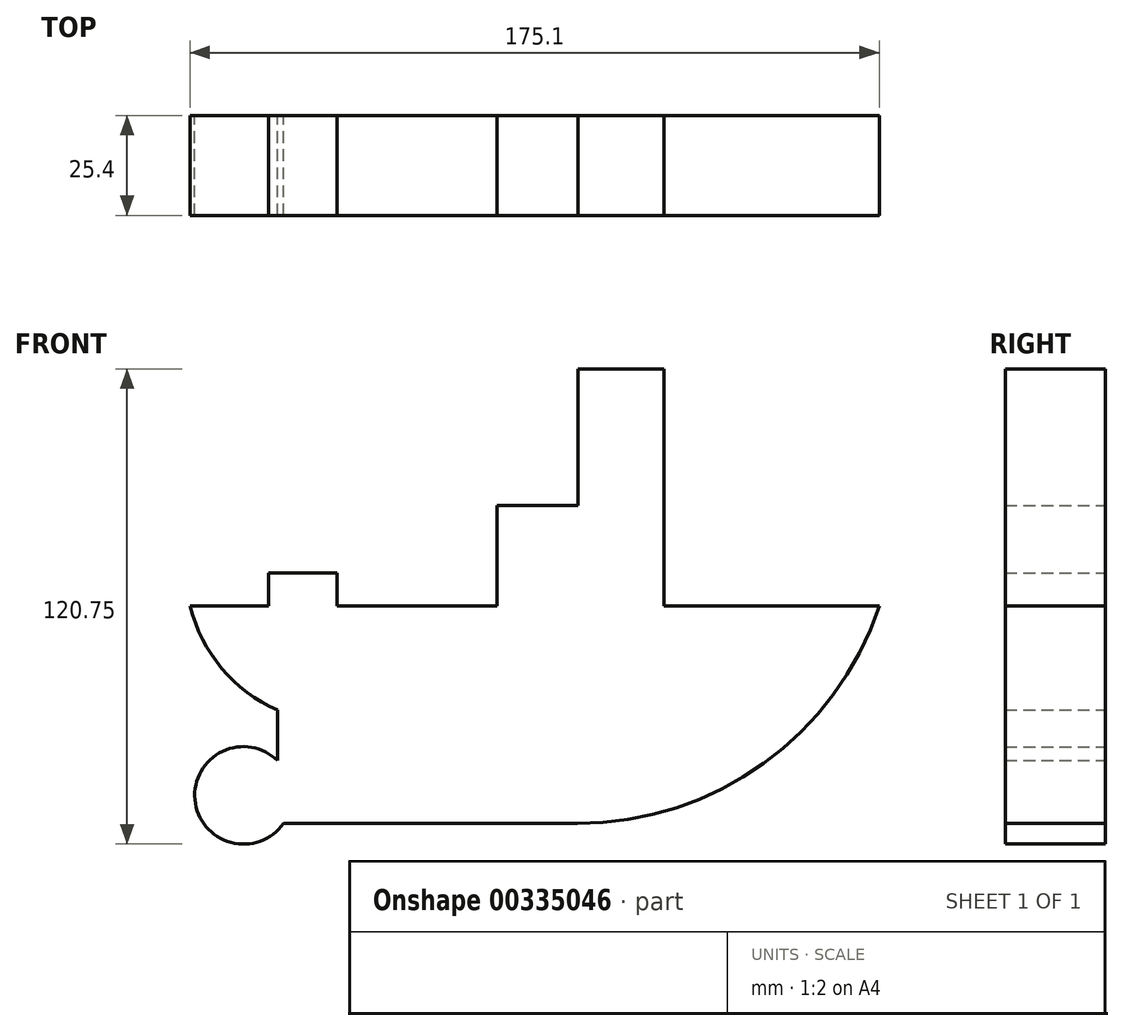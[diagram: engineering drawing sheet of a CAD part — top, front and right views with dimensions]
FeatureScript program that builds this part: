
annotation { "Feature Type Name" : "Feature", "Feature Type Description" : "" }
export const myFeature = defineFeature(function(context is Context, id is Id, definition is map)
    precondition{}
    {
        {
            var Q0;
            Q0=qCreatedBy(makeId("Front.planeOp"),FACE);
            var sketch = newSketch(context, id + "F0", { "sketchPlane" : qUnion([Q0])});
            skPoint(sketch, "E0", {"position": v(-98.45, 0) * mm});
            skPoint(sketch, "E1", {"position": v(0, -55.18) * mm});
            skPoint(sketch, "E2", {"position": v(76.65, 0) * mm});
            skArc(sketch, "E3", {"start": v(0, -55.18) * mm, "mid": v(47.23, -39.96) * mm, "end": v(76.65, 0) * mm});
            skLineSegment(sketch, "E4.bottom", {"start": v(0.03, 60.3) * mm, "end": v(21.93, 60.3) * mm});
            skLineSegment(sketch, "E4.top", {"start": v(0.03, 0) * mm, "end": v(21.93, 0) * mm});
            skLineSegment(sketch, "E4.left", {"start": v(0.03, 60.3) * mm, "end": v(0.03, 0) * mm});
            skLineSegment(sketch, "E4.right", {"start": v(21.93, 60.3) * mm, "end": v(21.93, 0) * mm});
            skLineSegment(sketch, "E5.bottom", {"start": v(0.03, 25.6) * mm, "end": v(-20.48, 25.6) * mm});
            skLineSegment(sketch, "E5.top", {"start": v(0.03, 0) * mm, "end": v(-20.48, 0) * mm});
            skLineSegment(sketch, "E5.left", {"start": v(0.03, 25.6) * mm, "end": v(0.03, 0) * mm});
            skLineSegment(sketch, "E5.right", {"start": v(-20.48, 25.6) * mm, "end": v(-20.48, 0) * mm});
            skLineSegment(sketch, "E6", {"start": v(0, 0) * mm, "end": v(-98.45, 0) * mm});
            skLineSegment(sketch, "E7", {"start": v(0.03, 0) * mm, "end": v(76.65, 0) * mm});
            skLineSegment(sketch, "E8.bottom", {"start": v(-61.07, 0) * mm, "end": v(-78.46, 0) * mm});
            skLineSegment(sketch, "E8.top", {"start": v(-61.07, 8.43) * mm, "end": v(-78.46, 8.43) * mm});
            skLineSegment(sketch, "E8.left", {"start": v(-61.07, 0) * mm, "end": v(-61.07, 8.43) * mm});
            skLineSegment(sketch, "E8.right", {"start": v(-78.46, 0) * mm, "end": v(-78.46, 8.43) * mm});
            skLineSegment(sketch, "E9.bottom", {"start": v(-76.23, -26.4) * mm, "end": v(0, -26.4) * mm});
            skLineSegment(sketch, "E9.top", {"start": v(-76.23, -55.18) * mm, "end": v(0, -55.18) * mm});
            skLineSegment(sketch, "E9.left", {"start": v(-76.23, -26.4) * mm, "end": v(-76.23, -39.23) * mm});
            skLineSegment(sketch, "E9.right", {"start": v(0, -26.4) * mm, "end": v(0, -55.18) * mm});
            skLineSegment(sketch, "E10", {"start": v(0, -26.4) * mm, "end": v(61.84, -26.4) * mm});
            skLineSegment(sketch, "E11", {"start": v(-76.23, 0) * mm, "end": v(-76.23, -26.4) * mm});
            skLineSegment(sketch, "E12", {"start": v(0.03, 0) * mm, "end": v(0, -26.4) * mm});
            skLineSegment(sketch, "E13", {"start": v(61.84, -26.4) * mm, "end": v(61.84, 0) * mm});
            skLineSegment(sketch, "E14", {"start": v(-76.23, -13.2) * mm, "end": v(61.84, -13.38) * mm});
            skLineSegment(sketch, "E15", {"start": v(-76.23, -39.23) * mm, "end": v(48.22, -39.23) * mm});
            skLineSegment(sketch, "E16", {"start": v(-76.23, -39.23) * mm, "end": v(-76.23, -55.18) * mm});
            skArc(sketch, "E17", {"start": v(-98.45, 0) * mm, "mid": v(-90.4, -15.78) * mm, "end": v(-76.23, -26.4) * mm});
            skArc(sketch, "E18", {"start": v(-76.23, -39.23) * mm, "mid": v(-97.23, -49.2) * mm, "end": v(-74.77, -55.18) * mm});
            skPoint(sketch, "E18.second.point", {"position": v(-97.26, -47.31) * mm});
            skSolve(sketch);
        }
        {
            var Q0;
            Q0 = qSketchRegion(id + "F0", true);
            extrude(context, id + "F1", {"entities" : qUnion([Q0]), "depth" : 25.4 * mm});
        }
    });
